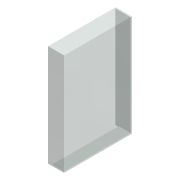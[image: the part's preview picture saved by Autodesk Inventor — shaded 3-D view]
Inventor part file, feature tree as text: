
AUTODESK INVENTOR PART (.ipt)
format: ipt  version: 2022 (Build 260153000, 153)  size: 130,560 bytes
history: native  units: mm
features: sketch x5, extrude x3, hole x2, other x1
ambient origin geometry x8: Origin, YZ Plane, XZ Plane, XY Plane, X Axis, Y Axis, Z Axis, Center Point
bodies: Body1 (feature_tree)
feature tree (11):
  other  "Твердое тело1"
  extrude  "Выдавливание1"  Depth=400.0mm
  extrude  "Выдавливание2"  Depth=600.0mm
  extrude  "Выдавливание3"  Depth=4.0mm TaperAngle=0.0deg
  hole  "Отверстие1"  [1 undecoded]
  hole  "Отверстие2"  [1 undecoded]
  sketch  "Эскиз1"
  sketch  "Эскиз2"
  sketch  "Эскиз3"
  sketch  "Эскиз4"
  sketch  "Эскиз5"
note: 2 required parameter values undecoded (feature->parameter linkage not recoverable at this tier; creation-order binding heuristic only, values carry confidence <= 0.55)
